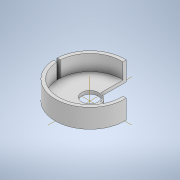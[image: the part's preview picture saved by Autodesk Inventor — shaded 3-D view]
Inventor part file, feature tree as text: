
AUTODESK INVENTOR PART (.ipt)
format: ipt  version: 2022 (Build 260153000, 153)  size: 173,568 bytes
history: native  units: in
note: dims shown in document units (in); Inventor stores cm internally (conversion verified against a paired STEP export)
features: extrude x2, chamfer x1, sketch x1
ambient origin geometry x8: Origin, YZ Plane, XZ Plane, XY Plane, X Axis, Y Axis, Z Axis, Center Point
bodies: Body1 (feature_tree)
feature tree (4):
  extrude  "Extrusion5"  Depth=0.0787in
  chamfer  "Chamfer1"  Distance=0.0394in
  extrude  "Extrusion8"  Depth=0.0787in
  sketch  "Sketch9"  dims[d30=1.6535in d31=0.0394in d32=0.0394in d33=0.0394in d34=0.0394in d35=0.3937in d36=0.0787in d37=0.0in d38=0.4724in d39=0.0197in d40=0.0394in d41=45.0deg d42=0.0787in d50=0.0787in d53=1.4961in d58=1.6535in d60=0.748in d61=0.4528in d62=0.0in d63=0.0787in d64=0.0787in d65=0.0787in d23=0.5in d24=0.0344in d25=0.5in d26=0.0344in d43=0.0in d44=0.0in d45=0.0in]
